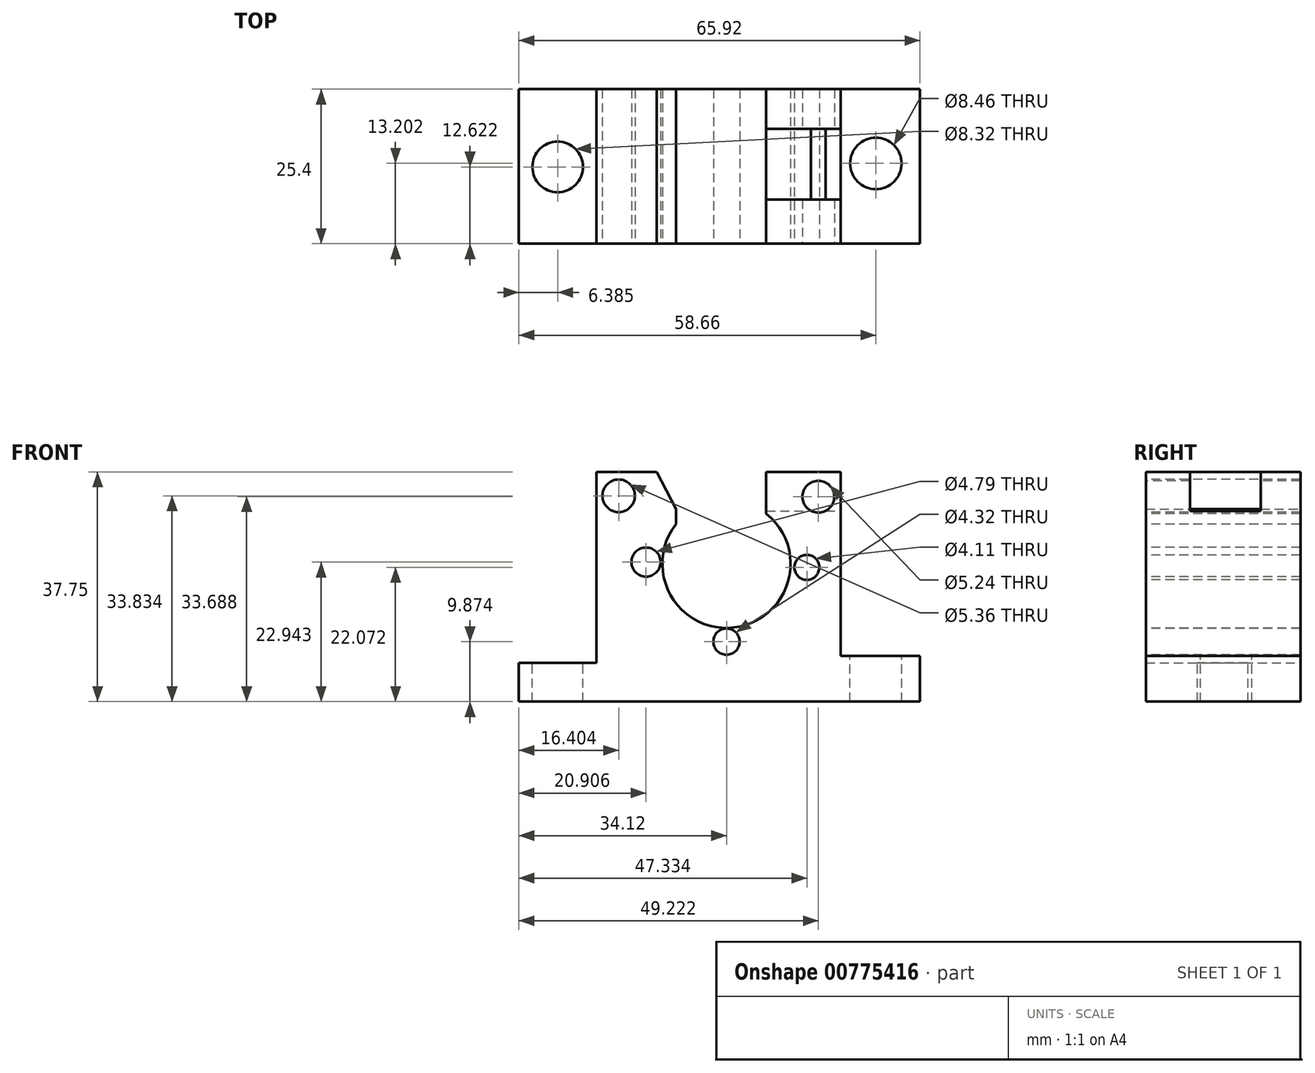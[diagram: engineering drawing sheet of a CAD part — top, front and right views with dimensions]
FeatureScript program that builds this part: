
annotation { "Feature Type Name" : "Feature", "Feature Type Description" : "" }
export const myFeature = defineFeature(function(context is Context, id is Id, definition is map)
    precondition{}
    {
        {
            var Q0;
            Q0=qCreatedBy(makeId("Front.planeOp"),FACE);
            var sketch = newSketch(context, id + "F0", { "sketchPlane" : qUnion([Q0])});
            skLineSegment(sketch, "E0", {"start": v(-21.35, 0) * mm, "end": v(-21.35, 14.81) * mm});
            skLineSegment(sketch, "E1", {"start": v(-21.35, 0) * mm, "end": v(0, 0) * mm});
            skLineSegment(sketch, "E2", {"start": v(0, 0) * mm, "end": v(18.73, 0) * mm});
            skLineSegment(sketch, "E3", {"start": v(18.73, 0) * mm, "end": v(18.73, 37.75) * mm});
            skLineSegment(sketch, "E4", {"start": v(18.73, 37.75) * mm, "end": v(6.53, 37.75) * mm});
            skLineSegment(sketch, "E5", {"start": v(6.53, 37.75) * mm, "end": v(6.53, 28.06) * mm});
            skLineSegment(sketch, "E6", {"start": v(-21.35, 14.81) * mm, "end": v(-21.35, 37.75) * mm});
            skLineSegment(sketch, "E7", {"start": v(-21.35, 37.75) * mm, "end": v(-11.47, 37.75) * mm});
            skLineSegment(sketch, "E8", {"start": v(-11.47, 37.75) * mm, "end": v(-8.28, 31.66) * mm});
            skLineSegment(sketch, "E9", {"start": v(-8.28, 31.66) * mm, "end": v(-8.28, 28.06) * mm});
            skLineSegment(sketch, "E10", {"start": v(-8.28, 28.06) * mm, "end": v(6.53, 28.06) * mm});
            skLineSegment(sketch, "E11.bottom", {"start": v(-34.12, 6.39) * mm, "end": v(-21.35, 6.39) * mm});
            skLineSegment(sketch, "E11.top", {"start": v(-34.12, 0) * mm, "end": v(-21.35, 0) * mm});
            skLineSegment(sketch, "E11.left", {"start": v(-34.12, 6.39) * mm, "end": v(-34.12, 0) * mm});
            skLineSegment(sketch, "E11.right", {"start": v(-21.35, 6.39) * mm, "end": v(-21.35, 0) * mm});
            skLineSegment(sketch, "E12.bottom", {"start": v(18.73, 7.55) * mm, "end": v(31.8, 7.55) * mm});
            skLineSegment(sketch, "E12.top", {"start": v(18.73, 0) * mm, "end": v(31.8, 0) * mm});
            skLineSegment(sketch, "E12.left", {"start": v(18.73, 7.55) * mm, "end": v(18.73, 0) * mm});
            skLineSegment(sketch, "E12.right", {"start": v(31.8, 7.55) * mm, "end": v(31.8, 0) * mm});
            skSolve(sketch);
        }
        {
            var Q0;
            Q0 = qSketchRegion(id + "F0", true);
            extrude(context, id + "F1", {"entities" : qUnion([Q0]), "depth" : 25.4 * mm, "offsetDistance" : 25.4 * mm});
        }
        {
            var Q0;
            Q0=makeQuery(id+"F1.opExtrude","CAP_FACE",FACE,{"disambiguationData":[OSD([sQuery(id+"F0.wireOp",EDGE,"E0"),sQuery(id+"F0.wireOp",EDGE,"E1"),sQuery(id+"F0.wireOp",EDGE,"E2"),sQuery(id+"F0.wireOp",EDGE,"E3"),sQuery(id+"F0.wireOp",EDGE,"E4"),sQuery(id+"F0.wireOp",EDGE,"E5"),sQuery(id+"F0.wireOp",EDGE,"E6"),sQuery(id+"F0.wireOp",EDGE,"E7"),sQuery(id+"F0.wireOp",EDGE,"E8"),sQuery(id+"F0.wireOp",EDGE,"E9"),sQuery(id+"F0.wireOp",EDGE,"E10")])],"isStart":false});
            var sketch = newSketch(context, id + "F2", { "sketchPlane" : qUnion([Q0])});
            skCircle(sketch, "E13", {"center": v(0, 22.65) * mm, "radius": 10.53 * mm});
            skSolve(sketch);
        }
        {
            var Q0;
            Q0 = qSketchRegion(id + "F2", true);
            extrude(context, id + "F3", {"entities" : qUnion([Q0]), "operationType" : NewBodyOperationType.REMOVE, "endBound" : BoundingType.UP_TO_NEXT, "oppositeDirection" : true, "depth" : 25.4 * mm, "offsetDistance" : 25.4 * mm});
        }
        {
            var Q0;
            Q0=makeQuery(id+"F1.opExtrude","CAP_FACE",FACE,{"disambiguationData":[OSD([sQuery(id+"F0.wireOp",EDGE,"E0"),sQuery(id+"F0.wireOp",EDGE,"E1"),sQuery(id+"F0.wireOp",EDGE,"E2"),sQuery(id+"F0.wireOp",EDGE,"E3"),sQuery(id+"F0.wireOp",EDGE,"E4"),sQuery(id+"F0.wireOp",EDGE,"E5"),sQuery(id+"F0.wireOp",EDGE,"E6"),sQuery(id+"F0.wireOp",EDGE,"E7"),sQuery(id+"F0.wireOp",EDGE,"E8"),sQuery(id+"F0.wireOp",EDGE,"E9"),sQuery(id+"F0.wireOp",EDGE,"E10")])],"isStart":false});
            var sketch = newSketch(context, id + "F4", { "sketchPlane" : qUnion([Q0])});
            skCircle(sketch, "E14", {"center": v(13.21, 22.07) * mm, "radius": 2.05 * mm});
            skCircle(sketch, "E15", {"center": v(0, 9.87) * mm, "radius": 2.16 * mm});
            skCircle(sketch, "E16", {"center": v(-13.21, 22.94) * mm, "radius": 2.4 * mm});
            skSolve(sketch);
        }
        {
            var Q0;
            Q0 = qSketchRegion(id + "F4", true);
            extrude(context, id + "F5", {"entities" : qUnion([Q0]), "operationType" : NewBodyOperationType.REMOVE, "endBound" : BoundingType.UP_TO_NEXT, "oppositeDirection" : true, "depth" : 25.4 * mm, "offsetDistance" : 25.4 * mm});
        }
        {
            var Q0;
            Q0=makeQuery(id+"F1.opExtrude","SWEPT_FACE",FACE,{"disambiguationData":[OSD([sQuery(id+"F0.wireOp",EDGE,"E12.bottom")])]});
            var sketch = newSketch(context, id + "F6", { "sketchPlane" : qUnion([Q0])});
            skCircle(sketch, "E17", {"center": v(24.54, -12.2) * mm, "radius": 4.23 * mm});
            skCircle(sketch, "E18", {"center": v(-27.73, -12.78) * mm, "radius": 4.16 * mm});
            skSolve(sketch);
        }
        {
            var Q0;
            Q0 = qSketchRegion(id + "F6", true);
            var Q1;
            Q1=makeQuery(id+"F1.opExtrude","SWEPT_FACE",FACE,{"disambiguationData":[OSD([sQuery(id+"F0.wireOp",EDGE,"E1"),sQuery(id+"F0.wireOp",EDGE,"E2"),sQuery(id+"F0.wireOp",EDGE,"E11.top"),sQuery(id+"F0.wireOp",EDGE,"E12.top")])]});
            extrude(context, id + "F7", {"entities" : qUnion([Q0, Q1]), "operationType" : NewBodyOperationType.REMOVE, "endBound" : BoundingType.THROUGH_ALL, "oppositeDirection" : true, "depth" : 25.4 * mm, "offsetDistance" : 25.4 * mm});
        }
        {
            var Q0;
            Q0=makeQuery(id+"F1.opExtrude","CAP_FACE",FACE,{"disambiguationData":[OSD([sQuery(id+"F0.wireOp",EDGE,"E0"),sQuery(id+"F0.wireOp",EDGE,"E1"),sQuery(id+"F0.wireOp",EDGE,"E2"),sQuery(id+"F0.wireOp",EDGE,"E3"),sQuery(id+"F0.wireOp",EDGE,"E4"),sQuery(id+"F0.wireOp",EDGE,"E5"),sQuery(id+"F0.wireOp",EDGE,"E6"),sQuery(id+"F0.wireOp",EDGE,"E7"),sQuery(id+"F0.wireOp",EDGE,"E8"),sQuery(id+"F0.wireOp",EDGE,"E9"),sQuery(id+"F0.wireOp",EDGE,"E10"),sQuery(id+"F0.wireOp",EDGE,"E11.bottom"),sQuery(id+"F0.wireOp",EDGE,"E11.top"),sQuery(id+"F0.wireOp",EDGE,"E11.left"),sQuery(id+"F0.wireOp",EDGE,"E12.bottom"),sQuery(id+"F0.wireOp",EDGE,"E12.top"),sQuery(id+"F0.wireOp",EDGE,"E12.right")])],"isStart":false});
            var sketch = newSketch(context, id + "F8", { "sketchPlane" : qUnion([Q0])});
            skCircle(sketch, "E19", {"center": v(-17.72, 33.83) * mm, "radius": 2.68 * mm});
            skCircle(sketch, "E20", {"center": v(15.1, 33.69) * mm, "radius": 2.62 * mm});
            skSolve(sketch);
        }
        {
            var Q0;
            Q0 = qSketchRegion(id + "F8", true);
            extrude(context, id + "F9", {"entities" : qUnion([Q0]), "operationType" : NewBodyOperationType.REMOVE, "endBound" : BoundingType.UP_TO_NEXT, "oppositeDirection" : true, "depth" : 25.4 * mm, "offsetDistance" : 25.4 * mm});
        }
        {
            var Q0;
            Q0=makeQuery(id+"F1.opExtrude","SWEPT_FACE",FACE,{"disambiguationData":[OSD([sQuery(id+"F0.wireOp",EDGE,"E3")])]});
            var sketch = newSketch(context, id + "F10", { "sketchPlane" : qUnion([Q0])});
            skLineSegment(sketch, "E21.bottom", {"start": v(-18.15, 42.4) * mm, "end": v(-6.53, 42.4) * mm});
            skLineSegment(sketch, "E21.top", {"start": v(-18.15, 31.37) * mm, "end": v(-6.53, 31.37) * mm});
            skLineSegment(sketch, "E21.left", {"start": v(-18.15, 42.4) * mm, "end": v(-18.15, 31.37) * mm});
            skLineSegment(sketch, "E21.right", {"start": v(-6.53, 42.4) * mm, "end": v(-6.53, 31.37) * mm});
            skSolve(sketch);
        }
        {
            var Q0;
            Q0 = qSketchRegion(id + "F10", true);
            extrude(context, id + "F11", {"entities" : qUnion([Q0]), "operationType" : NewBodyOperationType.REMOVE, "endBound" : BoundingType.UP_TO_NEXT, "oppositeDirection" : true, "depth" : 25.4 * mm, "offsetDistance" : 25.4 * mm});
        }
    });
